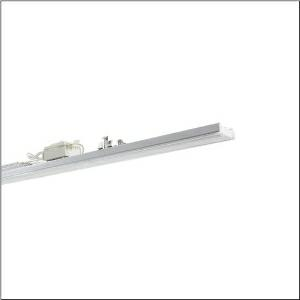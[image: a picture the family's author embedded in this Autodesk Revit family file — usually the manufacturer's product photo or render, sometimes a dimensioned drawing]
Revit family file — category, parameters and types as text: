
# Revit family: licross_r__11_recessed_mo_51te1edn495g_057d
name_source: partatom
category: Lighting Fixtures
units: mm (PartAtom-declared; Revit-internal decimal feet)

## family parameters
Cut with Voids When Loaded = No
Host = Face
Light Source = No
Part Type = Normal
Room Calculation Point = No
Round Connector Dimension = Use Diameter
Shared = No

## types (1)
- --- (1 x LED, 9900 lm, 56.7 W, 4000K)
    Apparent Load = 57 VA
    CIE Flux Codes = 85 95 99 100 100
    Color Rendering = 80
    Color Temperature = 4000K
    Default Elevation = 1800 mm
    Description = Licross® 11 Recessed MO, luminaire insert, of sheet steel, galvanised, coil coated, white, length: 1.500mm, width: 66mm, height: 67mm, LED rated luminous flux: 9.900lm, light colour: 840, control gear: DALI 2, with plug, 5-pole, with phase selection, mains connection: 220..240V, AC, 50/60Hz, rated input power: 57W, halogen-free wiring, primary light control with lens, of plastic, primary optical cover: cover, of PMMA, light emission: direct distribution, primary light characteristic: symmetric, protection rating (complete): IP54, insulation class (complete): insulation class I (protective earthing), certification: CE, ENEC, VDE, UKCA, protection symbol: D if used in an environment with non-conductive dust loads with corresponding accessories, impact resistance: IK06, permissible ambient temperature for indoor applications: -25..+35°C, corresponds to IFS (International Featured Standards) requirements for safety and quality in the food industry, reducing of maximum allowable ambient temperature of 5°C with ceiling mounting, LABS conformity tested according to VDMA 24364:2018-05, packaging unit: 1 piece
    Height = 58 mm
    Lamp = 1 x LED
    Lamp Light Flux = 9900 lm
    Lamp Power = 56.7 W
    Lamp count = 1
    Length = 1500 mm
    Luminous efficacy = 175 lm/W
    Manufacturer = Siteco
    ModVariant = No
    Model = 51TE1EDN495G
    Mounting Place = Ceiling
    Mounting Type = Pendant
    Number of Poles = 1
    OnlyDefault = Yes
    Power Factor = 1
    Product Name = Licross® 11 Recessed MO
    Product group = luminaire insert
    ProductGroupID = 902
    Protection Class = Protection class I
    Protection Degree = IP 54
    RLX_Detail_Level = 1
    RLX_Emergency_Light_Flux = 0 lm
    RLX_Emergency_Type = 0
    RLX_Emergency_Type_DB = No
    RlxData = <blob elided: 24613 chars, md5=a2651717>
    Socket = socket
    Standby Power = 0 W
    System Light Flux = 9900 lm
    System Power = 57 W
    Type Comments = factory setting: luminous flux: 100 % | dim-lin: 254 | 378 mA
    Type Image = l_1296930.jpg
    URL = http://relux.com
    VarID = @adj_095840
    Voltage = 0 V
    Weight = 0.00 kg
    Width = 66 mm

## geometry (parser evidence)
native form markers: Blend x4, Sweep x11
no freeform markers — native parametric forms only
